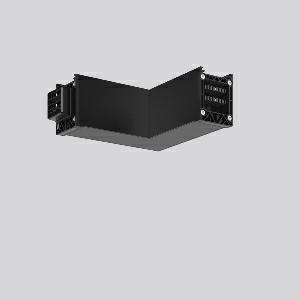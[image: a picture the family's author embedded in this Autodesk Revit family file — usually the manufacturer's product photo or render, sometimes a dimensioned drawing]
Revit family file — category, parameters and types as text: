
# Revit family: linedo_l-verbindung_982773_003_6_b6db
name_source: partatom
category: Lighting Fixtures
units: mm (PartAtom-declared; Revit-internal decimal feet)

## family parameters
Cut with Voids When Loaded = No
Host = Face
Light Source = No
Part Type = Normal
Room Calculation Point = No
Round Connector Dimension = Use Diameter
Shared = No

## types (1)
- LINEDO L-Verbindung
    Apparent Load = 0 VA
    Default Elevation = 1800 mm
    Description = Series: LINEDO
L-connector, 7-pole, connection plug / socket. Housing: extruded aluminium profile, powder-coated. Cover made of plastic, surface like housing. LINEDO plug system, plastic, black. Easy connection for rigid or flexible wires. 2 membrane cable entries (M25). Suitable for power supply in 7-pole version. Ready prewired. Colour-coded individual cables enable easy electromechanical separation.
Colour: jet black (RAL 9005)
Length: 204 mm
Width: 185 mm
Height: 76 mm
Weight: 640 g
    Height = 76 mm
    Lamp = 0 x
    Length = 204 mm
    Luminous efficacy = 0 lm/W
    Manufacturer = RZB
    ModVariant = No
    Model = 982773.003.6
    Mounting Place = Ceiling
    Mounting Type = Surface mounted
    Number of Poles = 1
    OnlyDefault = Yes
    Power Factor = 1
    Product Name = LINEDO L-Verbindung
    Product group = Surface mounted continuous line luminaire system
    ProductGroupID = 310
    Protection Class = Protection class I
    Protection Degree = Degree of protection
    RLX_Detail_Level = 1
    RLX_Emergency_Light_Flux = 0 lm
    RLX_Emergency_Type = 0
    RLX_Emergency_Type_DB = No
    RlxData = <blob elided: 19421 chars, md5=3e5278af>
    Standby Power = 0 W
    System Light Flux = 0 lm
    System Power = 0 W
    Type Comments = Product without accessories
    Type Image = 982773.003.jpg
    URL = http://relux.com
    VarID = ---
    Voltage = 0 V
    Weight = 0.00 kg
    Width = 185 mm

## geometry (parser evidence)
native form markers: Blend x4, Sweep x11
no freeform markers — native parametric forms only
